# Revit family: PRD_FrankeWS_WtrSplyFitngsForWshBsnsAndTrghs_PillarTap_F3EV1001-F3EV1009
name_source: partatom
category: Plumbing Fixtures
revit_build: Autodesk Revit 2018 (Build: 20190510_1515(x64)
units: mm (PartAtom-declared; Revit-internal decimal feet)

## family parameters
Always vertical = Yes
Cut with Voids When Loaded = No
OmniClass Number = 23.45.55.14
OmniClass Title = Single Faucets
Part Type = Normal
Room Calculation Point = No
Round Connector Dimension = Use Diameter
Shared = No
Work Plane-Based = No

## types (8) — shared parameters
AssetType = Fixed
Category = Pr_40_20_87_98, Washbasin taps
Color = Chrome
DefaultAutomaticHygieneFlushing = 24H-AFTER-ACTIVITY
Depressurised = no
DurationUnit = year
FaucetFunction = MIXED
FaucetMaterial = PRD_AR_StainlessSteel_PolishedFinished
FaucetOperation = SELFCLOSING
FaucetType = PILLAR
Finish = high-polished chromium-plated brass
FlowColdWater = 0.1 L/s
Form = Self-closing
FunctionalPrinciple = ELECTRONIX-C
HygieneFlushing = yes
IfcExportAs = IfcValveType
IfcExportType = FAUCET
InletSize = G 3/8
Manufacturer = KWC Group AG
ManufacturerName = KWC Group AG
ManufacturerURL = www.kwc.com
Material = Brass
MaterialsBody = Brass
MaterialsFinishAndColour = high-polished chromium-plated brass
MinimumFlowPressure = 1.00 bar
NBSDescription = Water supply fittings for wash basins and troughs
NBSReference = 45-35-70/371
NominalDiameter = 15 mm
PositionOfPowerConnection = BOTTOM
PowerConsumption = 1.5
ProductInformation = https://pim.kwc.com
ProtectiveShutdown = yes
ProtectiveSystemIP = 59K
SensorMaterial = <By Category>
SoundInsulation = no
SpoutProjection = 100.00 mm
ThermalDisinfection = no
TypeOfMixing = no
TypeOfMounting = TAPHOLE
TypeOfOperation = SENSOR-OPERATION
TypeOfSensor = OPTO-ELEC-SENSOR
TypeOfTap = PILLAR-TAP
URL = www.kwc.com
Uniclass2015Code = Pr_40_20_87_98
Uniclass2015Title = Washbasin taps
Uniclass2015Version = Products v1.7
Version = 1
WarrantyDurationUnit = year
zero-valued in all types: NominalHeight, NominalLength, NominalWidth

## per-type parameters (varying)
| type | BIMObjectName | Description | FlowRateMaximum | GrossWeight | Model | ModelNumber | ModelReference | Name | NetWeight | PowerSupplyConnection |
| F3EV1001 - 0.1 L/s with 6 V lithium battery | PRD_AR_WaterSupplyFittingsForWashBasinsAndTroughs_PillarTap_F3EV1001 | F3E pillar tap DN 15 for sanitary facilities, opto-electronically controlled. For connection to pre-mixed hot or cold water via hose and strainer. Control electronics, solenoid valve cartridge and sensor in all-metal housing, high-polished chromium-plated brass. Aerator with integrated flow regulator 6.0 l/min. Activated water hygiene flushing 24 hours after last activation, safety switch-off with continuous reflection and saving of statistical data. With option for parameterization and communication via optional, bidirectional remote control. With battery compartment including 6 V lithium battery (CR-P2) for installation under the washbasin. | 0.1 L/s at 3 bar | 1.38 kg | F3EV1001 | 2030033385 | F3EV1001 | F3 pillar tap F3EV1001 | 1.30 kg | Battery-6-V |
| F3EV1002 - 0.1 L/s with 100 - 240 V AC plug-in power supply unit | PRD_AR_WaterSupplyFittingsForWashBasinsAndTroughs_PillarTap_F3EV1002 | F3E pillar tap DN 15 for sanitary facilities, opto-electronically controlled. For connection to pre-mixed hot or cold water via hose and strainer. Control electronics, solenoid valve cartridge and sensor in all-metal housing, high-polished chromium-plated brass. Aerator with integrated flow regulator 6.0 l/min. Activated water hygiene flushing 24 hours after last activation, safety switch-off with continuous reflection and saving of statistical data. With option for parameterization and communication via optional, bidirectional remote control. With 100 - 240 V AC plug-in power supply unit. | 0.1 L/s at 3 bar | 1.40 kg | F3EV1002 | 2030033387 | F3EV1002 | F3 pillar tap F3EV1002 | 1.33 kg | 100-240VAC |
| F3EV1003 - 0.1 L/s with in-wall power supply 100 - 240 V AC | PRD_AR_WaterSupplyFittingsForWashBasinsAndTroughs_PillarTap_F3EV1003 | F3E pillar tap DN 15 for sanitary facilities, opto-electronically controlled. For connection to pre-mixed hot or cold water via hose and strainer. Control electronics, solenoid valve cartridge and sensor in all-metal housing, high-polished chromium-plated brass. Aerator with integrated flow regulator 6.0 l/min. Activated water hygiene flushing 24 hours after last activation, safety switch-off with continuous reflection and saving of statistical data. With option for parameterization and communication via optional, bidirectional remote control. With in-wall power supply 100 - 240 V AC. | 0.1 L/s at 3 bar | 1.40 kg | F3EV1003 | 2030033544 | F3EV1003 | F3 pillar tap F3EV1003 | 1.33 kg | 100-240VAC |
| F3EV1005 - 0.1 L/s with separate power supply via power supply unit 6.75 V / 12 V DC | PRD_AR_WaterSupplyFittingsForWashBasinsAndTroughs_PillarTap_F3EV1005 | F3E pillar tap DN 15 for sanitary facilities, opto-electronically controlled. For connection to pre-mixed hot or cold water via hose and strainer. Control electronics, solenoid valve cartridge and sensor in all-metal housing, high-polished chromium-plated brass. Aerator with integrated flow regulator 6.0 l/min. Activated water hygiene flushing 24 hours after last activation, safety switch-off with continuous reflection and saving of statistical data. With option for parameterization and communication via optional, bidirectional remote control. Separate power supply via power supply unit 6.75 V / 12 V DC. | 0.1 L/s at 3 bar | 1.30 kg | F3EV1005 | 2030039459 | F3EV1005 | F3 pillar tap F3EV1005 | 1.24 kg | 6 V DC - 12 V DC |
| F3EV1006 - 0.05 L/s with 6 V lithium battery | PRD_AR_WaterSupplyFittingsForWashBasinsAndTroughs_PillarTap_F3EV1006 | F3E pillar tap DN 15 for sanitary facilities, opto-electronically controlled. For connection to pre-mixed hot or cold water via hose and strainer. Control electronics, solenoid valve cartridge and sensor in all-metal housing, high-polished chromium-plated brass. Aerator with integrated flow regulator 3.0 l/min. Activated water hygiene flushing 24 hours after last activation, safety switch-off with continuous reflection and saving of statistical data. With option for parameterization and communication via optional, bidirectional remote control. With battery compartment including 6 V lithium battery (CR-P2) for installation under the washbasin. | 0.05 L/s at 3 bar | 1.40 kg | F3EV1006 | 2030039462 | F3EV1006 | F3 pillar tap F3EV1006 | 1.33 kg | Battery-6-V |
| F3EV1007 - 0.05 L/s with 100 - 240 V AC plug-in power supply unit | PRD_AR_WaterSupplyFittingsForWashBasinsAndTroughs_PillarTap_F3EV1007 | F3E pillar tap DN 15 for sanitary facilities, opto-electronically controlled. For connection to pre-mixed hot or cold water via hose and strainer. Control electronics, solenoid valve cartridge and sensor in all-metal housing, high-polished chromium-plated brass. Aerator with integrated flow regulator 3.0 l/min. Activated water hygiene flushing 24 hours after last activation, safety switch-off with continuous reflection and saving of statistical data. With option for parameterization and communication via optional, bidirectional remote control. With 100 - 240 V AC plug-in power supply unit. | 0.05 L/s at 3 bar | 1.30 kg | F3EV1007 | 2030039463 | F3EV1007 | F3 pillar tap F3EV1007 | 1.24 kg | 100-240VAC |
| F3EV1008 - 0.05 L/s with in-wall power supply 100 - 240 V AC | PRD_AR_WaterSupplyFittingsForWashBasinsAndTroughs_PillarTap_F3EV1008 | F3E pillar tap DN 15 for sanitary facilities, opto-electronically controlled. For connection to pre-mixed hot or cold water via hose and strainer. Control electronics, solenoid valve cartridge and sensor in all-metal housing, high-polished chromium-plated brass. Aerator with integrated flow regulator 3.0 l/min. Activated water hygiene flushing 24 hours after last activation, safety switch-off with continuous reflection and saving of statistical data. With option for parameterization and communication via optional, bidirectional remote control. With in-wall power supply 100 - 240 V AC. | 0.05 L/s at 3 bar | 1.46 kg | F3EV1008 | 2030039464 | F3EV1008 | F3 pillar tap F3EV1008 | 1.39 kg | 100-240VAC |
| F3EV1009 - 0.05 L/s with separate power supply via power supply unit 6.75 V / 12 V DC | PRD_AR_WaterSupplyFittingsForWashBasinsAndTroughs_PillarTap_F3EV1009 | F3E pillar tap DN 15 for sanitary facilities, opto-electronically controlled. For connection to pre-mixed hot or cold water via hose and strainer. Control electronics, solenoid valve cartridge and sensor in all-metal housing, high-polished chromium-plated brass. Aerator with integrated flow regulator 3.0 l/min. Activated water hygiene flushing 24 hours after last activation, safety switch-off with continuous reflection and saving of statistical data. With option for parameterization and communication via optional, bidirectional remote control. Separate power supply via power supply unit 6.75 V / 12 V DC. | 0.05 L/s at 3 bar | 1.30 kg | F3EV1009 | 2030039465 | F3EV1009 | F3 pillar tap F3EV1009 | 1.24 kg | 6 V DC - 12 V DC |

## geometry (parser evidence)
native form markers: Sweep x3
no freeform markers — native parametric forms only
